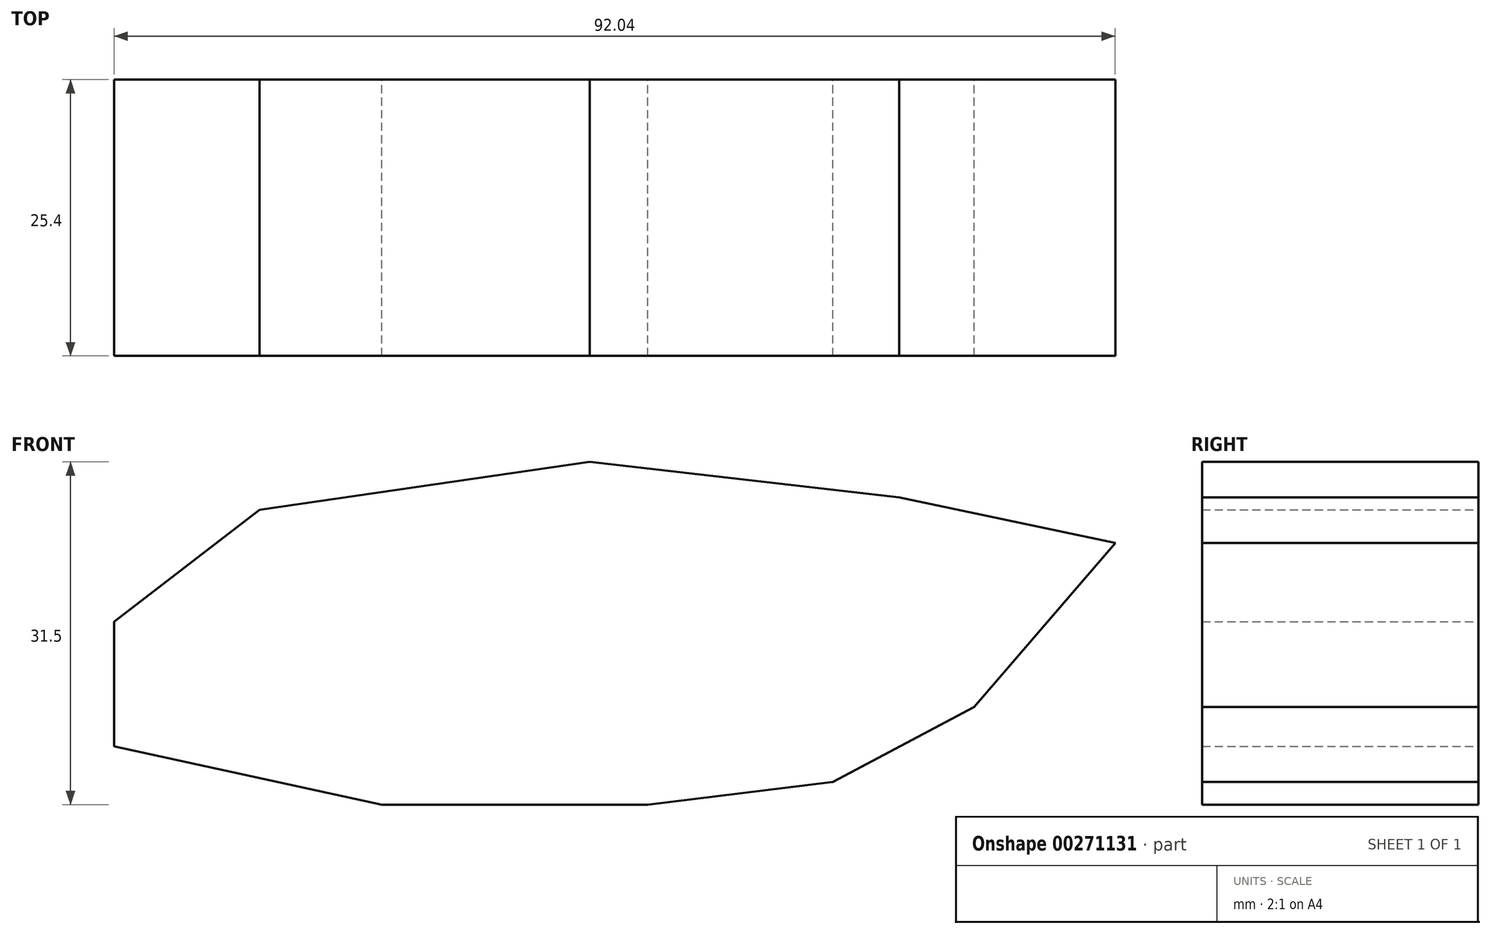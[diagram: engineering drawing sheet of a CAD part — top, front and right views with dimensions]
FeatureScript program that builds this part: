
annotation { "Feature Type Name" : "Feature", "Feature Type Description" : "" }
export const myFeature = defineFeature(function(context is Context, id is Id, definition is map)
    precondition{}
    {
        {
            var Q0;
            Q0=qCreatedBy(makeId("Front.planeOp"),FACE);
            var sketch = newSketch(context, id + "F0", { "sketchPlane" : qUnion([Q0])});
            skLineSegment(sketch, "E0", {"start": v(48.31, 37.24) * mm, "end": v(28.45, 41.44) * mm});
            skLineSegment(sketch, "E1", {"start": v(28.45, 41.44) * mm, "end": v(0, 44.68) * mm});
            skLineSegment(sketch, "E2", {"start": v(0, 44.68) * mm, "end": v(-30.36, 40.3) * mm});
            skLineSegment(sketch, "E3", {"start": v(-30.36, 40.3) * mm, "end": v(-43.73, 29.98) * mm});
            skLineSegment(sketch, "E4", {"start": v(-43.73, 29.98) * mm, "end": v(-43.73, 18.52) * mm});
            skLineSegment(sketch, "E5", {"start": v(-43.73, 18.52) * mm, "end": v(-19.1, 13.18) * mm});
            skLineSegment(sketch, "E6", {"start": v(-19.1, 13.18) * mm, "end": v(5.35, 13.18) * mm});
            skLineSegment(sketch, "E7", {"start": v(5.35, 13.18) * mm, "end": v(22.34, 15.28) * mm});
            skLineSegment(sketch, "E8", {"start": v(22.34, 15.28) * mm, "end": v(35.33, 22.15) * mm});
            skLineSegment(sketch, "E9", {"start": v(35.33, 22.15) * mm, "end": v(48.31, 37.24) * mm});
            skSolve(sketch);
        }
        {
            var Q0;
            Q0 = qSketchRegion(id + "F0", true);
            extrude(context, id + "F1", {"entities" : qUnion([Q0]), "depth" : 25.4 * mm});
        }
    });
